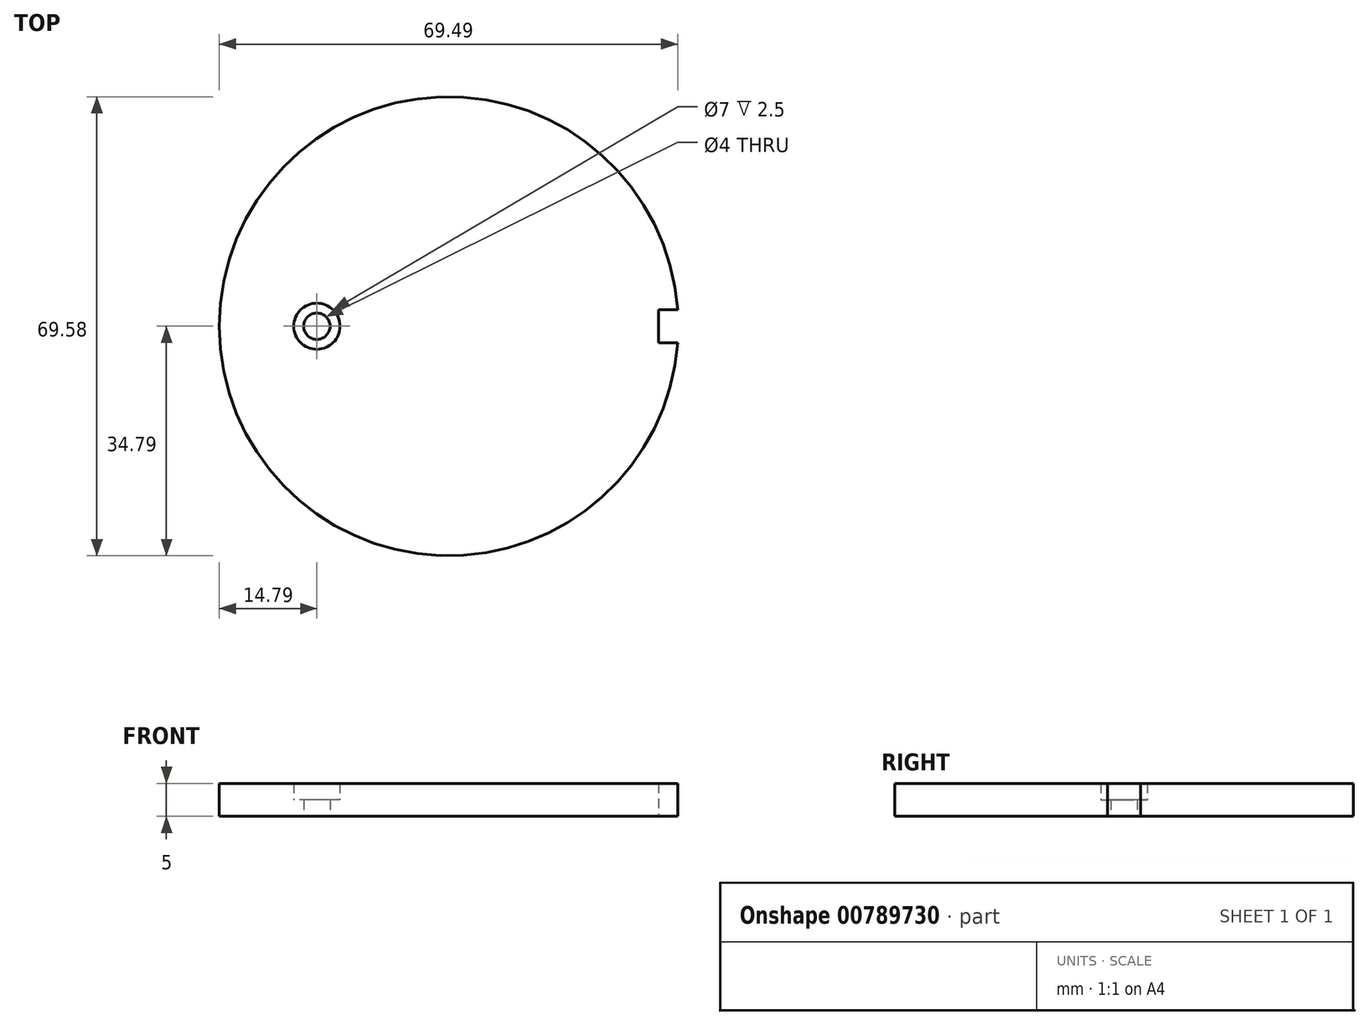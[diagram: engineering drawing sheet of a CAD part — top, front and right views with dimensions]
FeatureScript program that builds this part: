
annotation { "Feature Type Name" : "Feature", "Feature Type Description" : "" }
export const myFeature = defineFeature(function(context is Context, id is Id, definition is map)
    precondition{}
    {
        {
            var Q0;
            Q0=qCreatedBy(makeId("Top.planeOp"),FACE);
            var sketch = newSketch(context, id + "F0", { "sketchPlane" : qUnion([Q0])});
            skCircle(sketch, "E0", {"center": v(0, 0) * mm, "radius": 34.79 * mm});
            skCircle(sketch, "E1", {"center": v(-20, 0) * mm, "radius": 3.5 * mm});
            skCircle(sketch, "E2", {"center": v(-20, 0) * mm, "radius": 2 * mm});
            skLineSegment(sketch, "E3", {"start": v(31.79, 14.13) * mm, "end": v(31.79, -14.13) * mm});
            skLineSegment(sketch, "E4", {"start": v(34.7, 2.5) * mm, "end": v(31.79, 2.5) * mm});
            skLineSegment(sketch, "E5", {"start": v(34.7, -2.5) * mm, "end": v(31.79, -2.5) * mm});
            skSolve(sketch);
        }
        {
            var Q0;
            Q0=makeQuery(id+"F0.imprint","IMPRINT",FACE,{"disambiguationData":[TD([[makeQuery(id+"F0.imprint","IMPRINT",EDGE,{"derivedFrom":sQuery(id+"F0.wireOp",EDGE,"E1")}),-1.0]])]});
            var Q1;
            {var subQ3=sQuery(id+"F0.wireOp",EDGE,"E4");Q1=makeQuery(id+"F0.imprint","IMPRINT",FACE,{"disambiguationData":[TD([[makeQuery(id+"F0.imprint","IMPRINT",EDGE,{"derivedFrom":subQ3}),-1.0]])]});}
            var Q2;
            {var subQ3=sQuery(id+"F0.wireOp",EDGE,"E5");Q2=makeQuery(id+"F0.imprint","IMPRINT",FACE,{"disambiguationData":[TD([[makeQuery(id+"F0.imprint","IMPRINT",EDGE,{"derivedFrom":subQ3}),1.0]])]});}
            extrude(context, id + "F1", {"entities" : qUnion([Q0, Q1, Q2]), "depth" : 5 * mm, "offsetDistance" : 25 * mm});
        }
        {
            var Q0;
            Q0=makeQuery(id+"F0.imprint","IMPRINT",FACE,{"disambiguationData":[TD([[makeQuery(id+"F0.imprint","IMPRINT",EDGE,{"derivedFrom":sQuery(id+"F0.wireOp",EDGE,"E1")}),1.0]])]});
            extrude(context, id + "F2", {"entities" : qUnion([Q0]), "operationType" : NewBodyOperationType.ADD, "depth" : 2.5 * mm, "offsetDistance" : 25 * mm});
        }
    });
